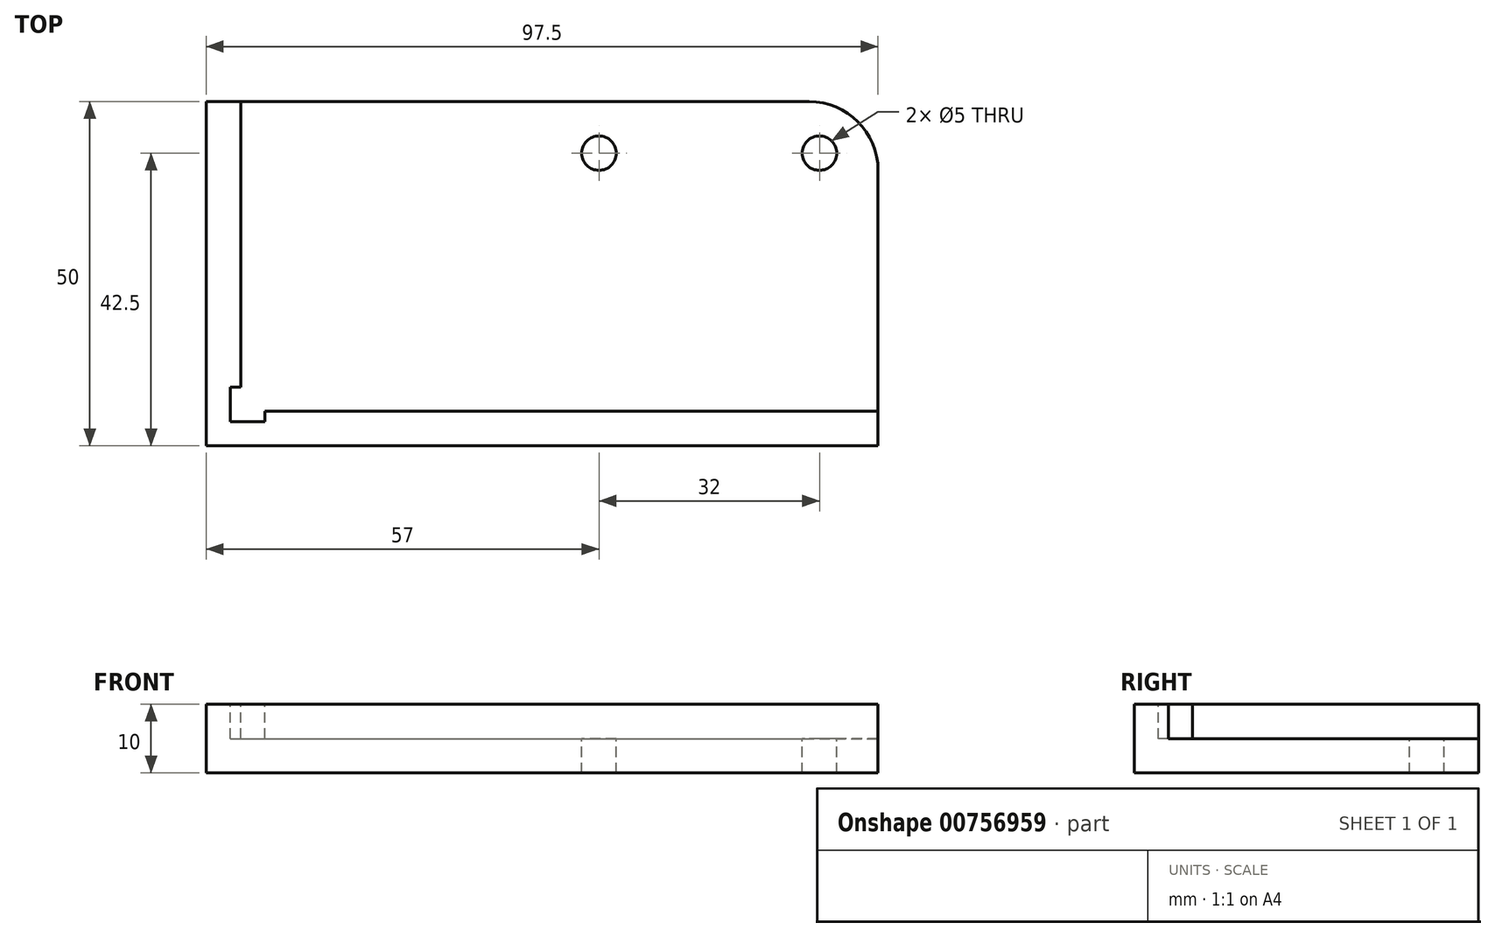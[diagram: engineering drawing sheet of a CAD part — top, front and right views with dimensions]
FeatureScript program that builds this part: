
annotation { "Feature Type Name" : "Feature", "Feature Type Description" : "" }
export const myFeature = defineFeature(function(context is Context, id is Id, definition is map)
    precondition{}
    {
        {
            var Q0;
            Q0=qCreatedBy(makeId("Top.planeOp"),FACE);
            var sketch = newSketch(context, id + "F0", { "sketchPlane" : qUnion([Q0])});
            skLineSegment(sketch, "E0.bottom", {"start": v(0, 0) * mm, "end": v(97.5, 0) * mm});
            skLineSegment(sketch, "E0.top", {"start": v(0, 50) * mm, "end": v(97.5, 50) * mm});
            skLineSegment(sketch, "E0.left", {"start": v(0, 0) * mm, "end": v(0, 50) * mm});
            skLineSegment(sketch, "E0.right", {"start": v(97.5, 0) * mm, "end": v(97.5, 50) * mm});
            skSolve(sketch);
        }
        {
            var Q0;
            Q0=makeQuery(id+"F0.imprint","IMPRINT",FACE,{"disambiguationData":[TD([[makeQuery(id+"F0.imprint","IMPRINT",EDGE,{"derivedFrom":sQuery(id+"F0.wireOp",EDGE,"E0.bottom")}),1.0]])]});
            extrude(context, id + "F1", {"entities" : qUnion([Q0]), "depth" : 10 * mm, "offsetDistance" : 25 * mm});
        }
        {
            var Q0;
            Q0=makeQuery(id+"F1.opExtrude","SWEPT_FACE",FACE,{"disambiguationData":[OSD([sQuery(id+"F0.wireOp",EDGE,"E0.right")])]});
            var Q1;
            Q1=makeQuery(id+"F1.opExtrude","SWEPT_FACE",FACE,{"disambiguationData":[OSD([sQuery(id+"F0.wireOp",EDGE,"E0.top")])]});
            var Q2;
            Q2=makeQuery(id+"F1.opExtrude","CAP_FACE",FACE,{"disambiguationData":[OSD([sQuery(id+"F0.wireOp",EDGE,"E0.bottom"),sQuery(id+"F0.wireOp",EDGE,"E0.top"),sQuery(id+"F0.wireOp",EDGE,"E0.left"),sQuery(id+"F0.wireOp",EDGE,"E0.right")])],"isStart":false});
            shell(context, id + "F2", {"entities" : qUnion([Q0, Q1, Q2]), "thickness" : 5 * mm});
        }
        {
            var Q0;
            Q0=makeQuery(id+"F1.opExtrude","CAP_FACE",FACE,{"disambiguationData":[OSD([sQuery(id+"F0.wireOp",EDGE,"E0.bottom"),sQuery(id+"F0.wireOp",EDGE,"E0.top"),sQuery(id+"F0.wireOp",EDGE,"E0.left"),sQuery(id+"F0.wireOp",EDGE,"E0.right")])],"isStart":false});
            var sketch = newSketch(context, id + "F3", { "sketchPlane" : qUnion([Q0])});
            skLineSegment(sketch, "E1.bottom", {"start": v(3.5, 8.5) * mm, "end": v(8.5, 8.5) * mm});
            skLineSegment(sketch, "E1.top", {"start": v(3.5, 3.5) * mm, "end": v(8.5, 3.5) * mm});
            skLineSegment(sketch, "E1.left", {"start": v(3.5, 8.5) * mm, "end": v(3.5, 3.5) * mm});
            skLineSegment(sketch, "E1.right", {"start": v(8.5, 8.5) * mm, "end": v(8.5, 3.5) * mm});
            skSolve(sketch);
        }
        {
            var Q0;
            Q0 = qSketchRegion(id + "F3", true);
            extrude(context, id + "F4", {"entities" : qUnion([Q0]), "operationType" : NewBodyOperationType.REMOVE, "oppositeDirection" : true, "depth" : 5 * mm, "offsetDistance" : 25 * mm});
        }
        {
            var Q0;
            Q0=makeQuery(id+"F4.boolean.opBoolean","MERGE",FACE,{"derivedFrom":[makeQuery(id+"F2.opShell","OFFSET_FACE",FACE,{"disambiguationData":[OSD([sQuery(id+"F0.wireOp",EDGE,"E0.bottom"),sQuery(id+"F0.wireOp",EDGE,"E0.top"),sQuery(id+"F0.wireOp",EDGE,"E0.left"),sQuery(id+"F0.wireOp",EDGE,"E0.right")])]})],"fromTools":[makeQuery(id+"F4.opExtrude","CAP_FACE",FACE,{"disambiguationData":[OSD([sQuery(id+"F3.wireOp",EDGE,"E1.bottom"),sQuery(id+"F3.wireOp",EDGE,"E1.top"),sQuery(id+"F3.wireOp",EDGE,"E1.left"),sQuery(id+"F3.wireOp",EDGE,"E1.right")])],"isStart":false})]});
            var sketch = newSketch(context, id + "F5", { "sketchPlane" : qUnion([Q0])});
            skPoint(sketch, "E2", {"position": v(57, 42.5) * mm});
            skPoint(sketch, "E3", {"position": v(89, 42.5) * mm});
            skLineSegment(sketch, "E4", {"start": v(57, 42.5) * mm, "end": v(89, 42.5) * mm, "construction": true});
            skSolve(sketch);
        }
        {
            var Q0;
            Q0=sQuery(id+"F5.wireOp",VERTEX,"E2");
            var Q1;
            Q1=sQuery(id+"F5.wireOp",VERTEX,"E3");
            var Q2;
            Q2=makeQuery(id+"F1.opExtrude","SWEPT_BODY",BODY,{"disambiguationData":[OSD([sQuery(id+"F0.wireOp",EDGE,"E0.bottom"),sQuery(id+"F0.wireOp",EDGE,"E0.top"),sQuery(id+"F0.wireOp",EDGE,"E0.left"),sQuery(id+"F0.wireOp",EDGE,"E0.right")])]});
            hole(context, id + "F6", {"style" : HoleStyle.SIMPLE, "endStyle" : HoleEndStyle.THROUGH, "holeDiameter" : 5 * mm, "majorDiameter" : 5 * mm, "isTappedThrough" : true, "tappedDepth" : 12 * mm, "tapClearance" : 3, "locations" : qUnion([Q0, Q1]), "scope" : qUnion([Q2])});
        }
        {
            var Q0;
            Q0=makeQuery(id+"F1.opExtrude","SWEPT_EDGE",EDGE,{"disambiguationData":[OSD([sQuery(id+"F0.wireOp",EDGE,"E0.top"),sQuery(id+"F0.wireOp",EDGE,"E0.right")])]});
            fillet(context, id + "F7", {"entities" : qUnion([Q0]), "tangentPropagation" : true, "radius" : 10 * mm, "defaultsChanged" : true, "vertexSettings" : [], "allowEdgeOverflow" : false});
        }
    });
